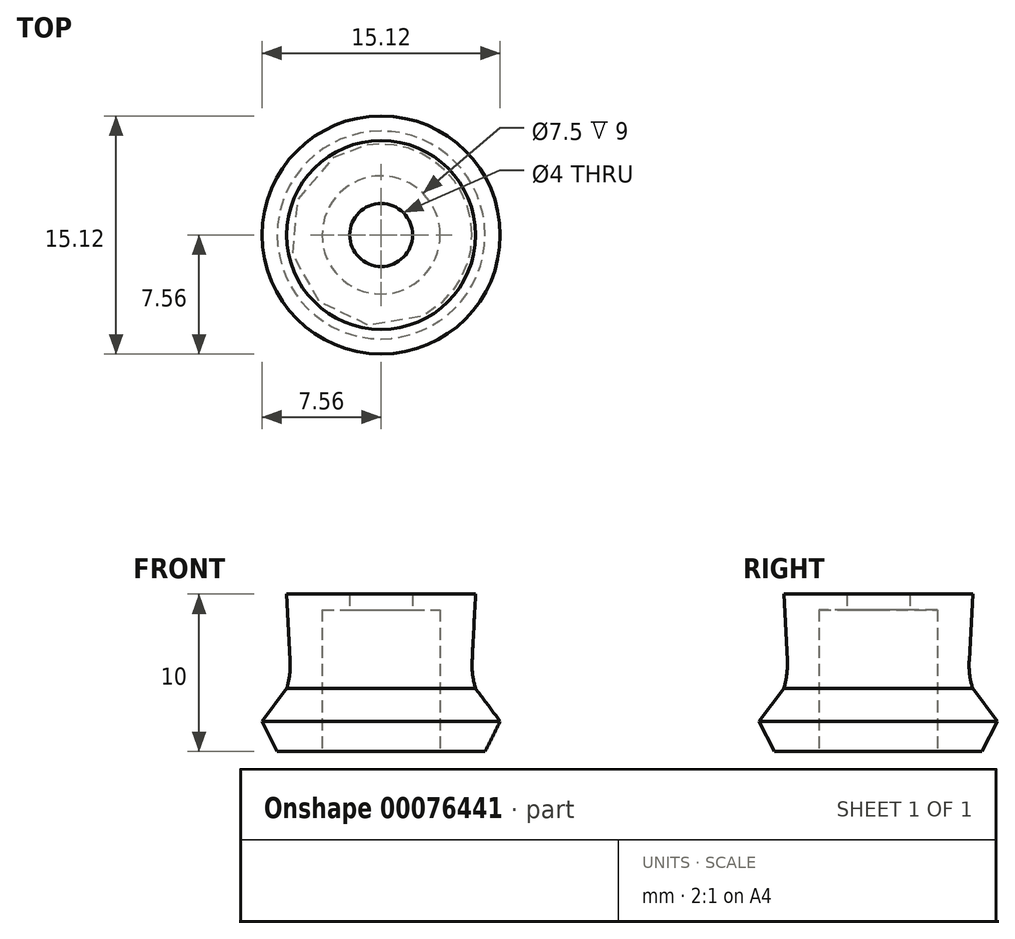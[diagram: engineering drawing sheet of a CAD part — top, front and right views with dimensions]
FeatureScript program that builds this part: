
annotation { "Feature Type Name" : "Feature", "Feature Type Description" : "" }
export const myFeature = defineFeature(function(context is Context, id is Id, definition is map)
    precondition{}
    {
        {
            var Q0;
            Q0=qCreatedBy(makeId("Top.planeOp"),FACE);
            var sketch = newSketch(context, id + "F0", { "sketchPlane" : qUnion([Q0])});
            skCircle(sketch, "E0", {"center": v(0, 0) * mm, "radius": 6 * mm});
            skSolve(sketch);
        }
        {
            var Q0;
            Q0 = qSketchRegion(id + "F0", true);
            extrude(context, id + "F1", {"entities" : qUnion([Q0]), "depth" : 10 * mm});
        }
        {
            var Q0;
            Q0=qCreatedBy(makeId("Right.planeOp"),FACE);
            var sketch = newSketch(context, id + "F2", { "sketchPlane" : qUnion([Q0])});
            skLineSegment(sketch, "E1", {"start": v(6, 4) * mm, "end": v(6, 0) * mm});
            skLineSegment(sketch, "E2", {"start": v(6, 4) * mm, "end": v(9, 0) * mm});
            skLineSegment(sketch, "E3", {"start": v(9, 0) * mm, "end": v(6, 0) * mm});
            skSolve(sketch);
        }
        {
            var Q0;
            Q0=makeQuery(id+"F2.imprint","IMPRINT",FACE,{"disambiguationData":[TD([[makeQuery(id+"F2.imprint","IMPRINT",EDGE,{"derivedFrom":sQuery(id+"F2.wireOp",EDGE,"E1")}),1.0]])]});
            var Q1;
            Q1=makeQuery(id+"F1.opExtrude","CAP_EDGE",EDGE,{"disambiguationData":[OSD([sQuery(id+"F0.wireOp",EDGE,"E0")])],"isStart":true});
            revolve(context, id + "F3", {"operationType" : NewBodyOperationType.ADD, "entities" : qUnion([Q0]), "axis" : qUnion([Q1]), "revolveType" : RevolveType.FULL});
        }
        {
            var Q0;
            Q0=makeQuery(id+"F3.boolean.opBoolean","MERGE",FACE,{"derivedFrom":[makeQuery(id+"F1.opExtrude","CAP_FACE",FACE,{"disambiguationData":[OSD([sQuery(id+"F0.wireOp",EDGE,"E0")])],"isStart":true}),makeQuery(id+"F3.opRevolve","SWEPT_FACE",FACE,{"disambiguationData":[OSD([sQuery(id+"F2.wireOp",EDGE,"E3")])]})]});
            var sketch = newSketch(context, id + "F4", { "sketchPlane" : qUnion([Q0])});
            skCircle(sketch, "E4", {"center": v(0, 0) * mm, "radius": 3.75 * mm});
            skSolve(sketch);
        }
        {
            var Q0;
            Q0 = qSketchRegion(id + "F4", true);
            extrude(context, id + "F5", {"entities" : qUnion([Q0]), "operationType" : NewBodyOperationType.REMOVE, "oppositeDirection" : true, "depth" : 9 * mm});
        }
        {
            var Q0;
            Q0=makeQuery(id+"F5.boolean.opBoolean","COPY",FACE,{"derivedFrom":makeQuery(id+"F5.opExtrude","CAP_FACE",FACE,{"disambiguationData":[OSD([sQuery(id+"F4.wireOp",EDGE,"E4")])],"isStart":false})});
            var sketch = newSketch(context, id + "F6", { "sketchPlane" : qUnion([Q0])});
            skPoint(sketch, "E5.center.orphan", {"position": v(-1.24, 0) * mm});
            skCircle(sketch, "E6", {"center": v(0, 0) * mm, "radius": 2 * mm});
            skSolve(sketch);
        }
        {
            var Q0;
            Q0 = qSketchRegion(id + "F6", true);
            extrude(context, id + "F7", {"entities" : qUnion([Q0]), "operationType" : NewBodyOperationType.REMOVE, "oppositeDirection" : true, "depth" : 3.5 * mm});
        }
        {
            var Q0;
            Q0=qCreatedBy(makeId("Front.planeOp"),FACE);
            var sketch = newSketch(context, id + "F8", { "sketchPlane" : qUnion([Q0])});
            skLineSegment(sketch, "E7", {"start": v(6, 10) * mm, "end": v(6, 4) * mm});
            skLineSegment(sketch, "E8.0", {"start": v(6, 4) * mm, "end": v(5.69, 4) * mm});
            skLineSegment(sketch, "E9", {"start": v(6, 10) * mm, "end": v(5.69, 4) * mm});
            skPoint(sketch, "E10.orphan", {"position": v(-6, 4) * mm});
            skSolve(sketch);
        }
        {
            var Q0;
            Q0 = qSketchRegion(id + "F8", true);
            var Q1;
            Q1=makeQuery(id+"F1.opExtrude","CAP_EDGE",EDGE,{"disambiguationData":[OSD([sQuery(id+"F0.wireOp",EDGE,"E0")])],"isStart":false});
            revolve(context, id + "F9", {"operationType" : NewBodyOperationType.REMOVE, "entities" : qUnion([Q0]), "axis" : qUnion([Q1]), "revolveType" : RevolveType.FULL, "oppositeDirection" : true});
        }
        {
            var Q0;
            Q0=makeQuery(id+"F9.boolean.opBoolean","COPY",EDGE,{"derivedFrom":makeQuery(id+"F9.opRevolve","SWEPT_EDGE",EDGE,{"disambiguationData":[OSD([sQuery(id+"F8.wireOp",EDGE,"E8.0"),sQuery(id+"F8.wireOp",EDGE,"E9")])]})});
            fillet(context, id + "F10", {"entities" : qUnion([Q0]), "radius" : 5.08 * mm, "tangentPropagation" : true, "allowEdgeOverflow" : false});
        }
        {
            var Q0;
            Q0=makeQuery(id+"F3.opRevolve","SWEPT_EDGE",EDGE,{"disambiguationData":[OSD([sQuery(id+"F2.wireOp",EDGE,"E2"),sQuery(id+"F2.wireOp",EDGE,"E3")])]});
            chamfer(context, id + "F11", {"entities" : qUnion([Q0]), "width" : 1.2 * mm, "tangentPropagation" : true});
        }
    });
